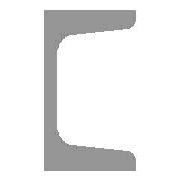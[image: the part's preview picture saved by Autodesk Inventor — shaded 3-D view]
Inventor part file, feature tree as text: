
AUTODESK INVENTOR PART (.ipt)
format: ipt  version: 2017 (Build 210142000, 142)  size: 141,312 bytes
history: native  units: mm (DEFAULTED — no unit token found)
features: other x4, plane x2, sketch x2, split x1
ambient origin geometry x8: Origin, YZ Plane, XZ Plane, XY Plane, X Axis, Y Axis, Z Axis, Center Point
bodies: Solid1 (feature_tree), Body (feature_tree)
feature tree (9):
  parser-record x1  (decoder bookkeeping rows leaked as tree rows — omitted from the tree; the rows remain in map.json)
  other  "Driven Length"
  other  "Start plane"
  other  "End plane"
  plane  "Work Plane4"
  split  "Split1"
  sketch  "Sketch3"  dims[d0=4.6736mm]
  plane  "Work Plane3"
  sketch  "Sketch4"  dims[d1=50.8mm d2=40.2336mm d3=7.5184mm d4=17.682845mm d5=0.926581mm d6=2438.4mm d7=0.0mm d25=0.0mm d26=-0.0mm d27=2438.4mm d28=6.712646mm d29=2.2352mm d30=90.0deg d31=2438.4mm]
